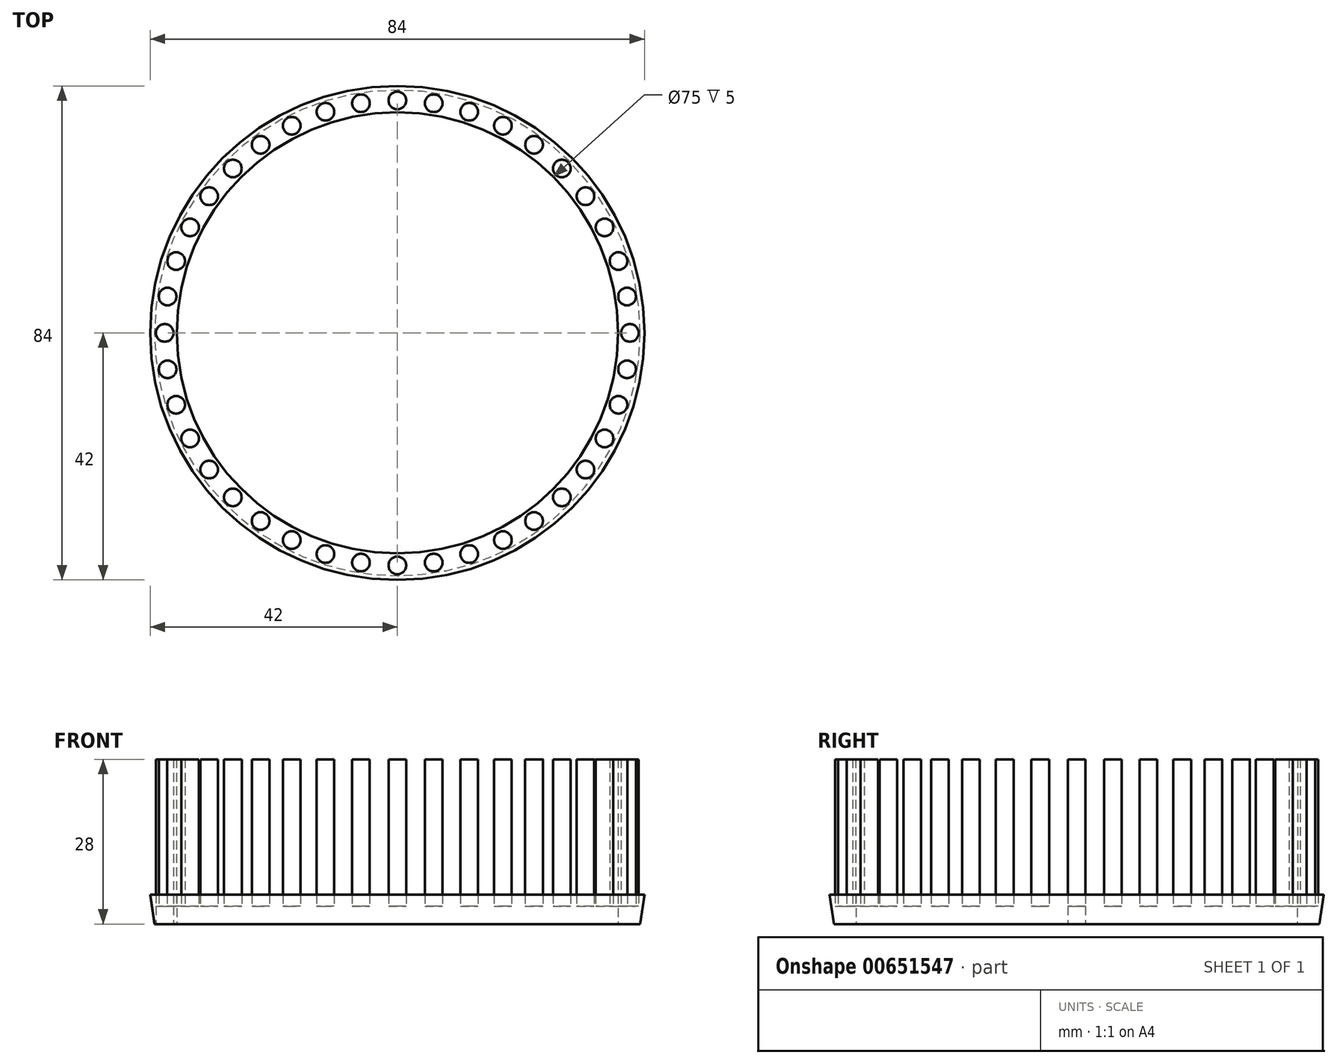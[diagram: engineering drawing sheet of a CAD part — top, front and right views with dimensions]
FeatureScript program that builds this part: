
annotation { "Feature Type Name" : "Feature", "Feature Type Description" : "" }
export const myFeature = defineFeature(function(context is Context, id is Id, definition is map)
    precondition{}
    {
        {
            var Q0;
            Q0=qCreatedBy(makeId("Front.planeOp"),FACE);
            var sketch = newSketch(context, id + "F0", { "sketchPlane" : qUnion([Q0])});
            skLineSegment(sketch, "E0", {"start": v(-41.27, 0) * mm, "end": v(0, 0) * mm});
            skLineSegment(sketch, "E1", {"start": v(0, 0) * mm, "end": v(0, 5) * mm});
            skLineSegment(sketch, "E2", {"start": v(0, 5) * mm, "end": v(-42, 5) * mm});
            skLineSegment(sketch, "E3", {"start": v(-42, 5) * mm, "end": v(-41.27, 0) * mm});
            skSolve(sketch);
        }
        {
            var Q0;
            Q0 = qSketchRegion(id + "F0", true);
            var Q1;
            Q1=sQuery(id+"F0.wireOp",EDGE,"E1");
            revolve(context, id + "F1", {"entities" : qUnion([Q0]), "axis" : qUnion([Q1]), "revolveType" : RevolveType.FULL});
        }
        {
            var Q0;
            Q0=qCreatedBy(makeId("Top.planeOp"),FACE);
            var sketch = newSketch(context, id + "F2", { "sketchPlane" : qUnion([Q0])});
            skCircle(sketch, "E4", {"center": v(0, 0) * mm, "radius": 37.5 * mm});
            skSolve(sketch);
        }
        {
            var Q0;
            Q0 = qSketchRegion(id + "F2", true);
            extrude(context, id + "F3", {"entities" : qUnion([Q0]), "operationType" : NewBodyOperationType.REMOVE, "depth" : 25 * mm, "offsetDistance" : 25 * mm});
        }
        {
            var Q0;
            Q0=qCreatedBy(makeId("Front.planeOp"),FACE);
            var sketch = newSketch(context, id + "F4", { "sketchPlane" : qUnion([Q0])});
            skLineSegment(sketch, "E5", {"start": v(-39.53, 0) * mm, "end": v(-41.03, 0) * mm});
            skLineSegment(sketch, "E6", {"start": v(-41.03, 0) * mm, "end": v(-41.03, 3) * mm});
            skLineSegment(sketch, "E7", {"start": v(-39.53, 0) * mm, "end": v(-39.53, 3) * mm});
            skLineSegment(sketch, "E8", {"start": v(-39.53, 3) * mm, "end": v(-41.03, 3) * mm});
            skSolve(sketch);
        }
        {
            var Q0;
            Q0 = qSketchRegion(id + "F4", true);
            var Q1;
            Q1=sQuery(id+"F4.wireOp",EDGE,"E7");
            revolve(context, id + "F5", {"entities" : qUnion([Q0]), "axis" : qUnion([Q1]), "revolveType" : RevolveType.FULL});
        }
        {
            var Q0;
            Q0=makeQuery(id+"F5.opRevolve","SWEPT_FACE",FACE,{"disambiguationData":[OSD([sQuery(id+"F4.wireOp",EDGE,"E8")])]});
            extrude(context, id + "F6", {"entities" : qUnion([Q0]), "depth" : 25 * mm, "offsetDistance" : 25 * mm});
        }
        {
            var Q0;
            Q0=makeQuery(id+"F6.opExtrude","SWEPT_BODY",BODY,{"disambiguationData":[OSD([sQuery(id+"F4.wireOp",EDGE,"E8")])]});
            var Q1;
            Q1=sQuery(id+"F0.wireOp",EDGE,"E1");
            circularPattern(context, id + "F7", {"entities" : qUnion([Q0]), "axis" : qUnion([Q1]), "angle" : 360 * degree, "instanceCount" : 40, "equalSpace" : true});
        }
    });
